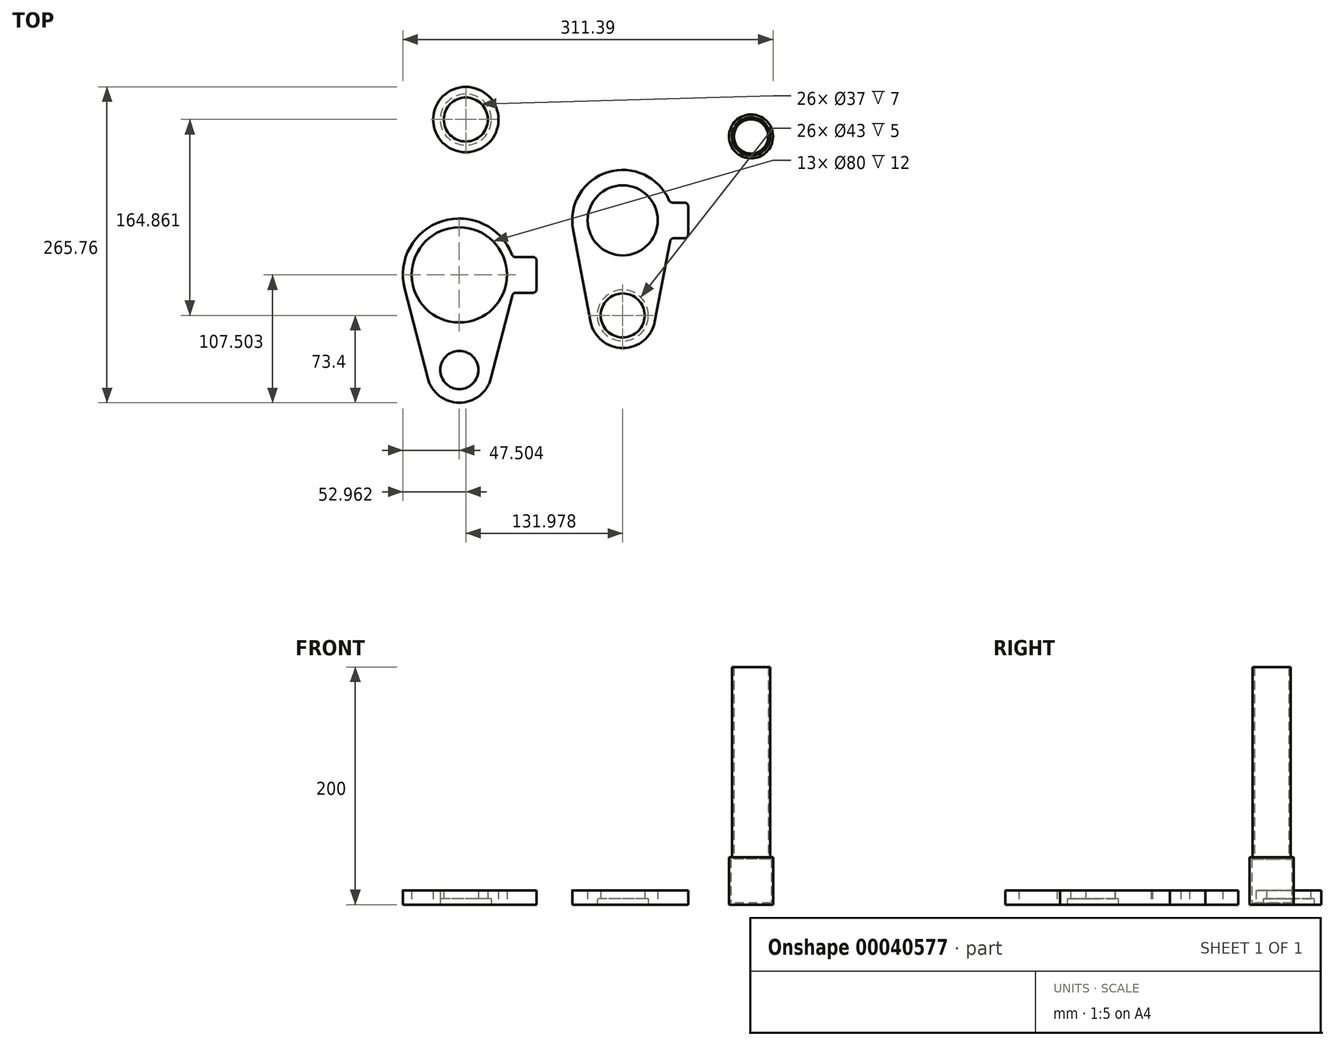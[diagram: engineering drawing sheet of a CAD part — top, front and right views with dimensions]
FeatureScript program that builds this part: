
annotation { "Feature Type Name" : "Feature", "Feature Type Description" : "" }
export const myFeature = defineFeature(function(context is Context, id is Id, definition is map)
    precondition{}
    {
        {
            var Q0;
            Q0=qCreatedBy(makeId("Top.planeOp"),FACE);
            var sketch = newSketch(context, id + "F0", { "sketchPlane" : qUnion([Q0])});
            skArc(sketch, "E0", {"start": v(29.46, 1.5) * mm, "mid": v(-29.5, 0) * mm, "end": v(29.46, -1.5) * mm});
            skArc(sketch, "E1", {"start": v(39.03, 16.81) * mm, "mid": v(-12.47, 40.63) * mm, "end": v(-41.75, -7.97) * mm});
            skCircle(sketch, "E2", {"center": v(0, -80) * mm, "radius": 18.5 * mm});
            skArc(sketch, "E3", {"start": v(-27.01, -85.16) * mm, "mid": v(0, -107.5) * mm, "end": v(27.01, -85.16) * mm});
            skLineSegment(sketch, "E4.left", {"start": v(55, 12) * mm, "end": v(55, 1.5) * mm});
            skLineSegment(sketch, "E5", {"start": v(52, 15) * mm, "end": v(41.79, 15) * mm});
            skLineSegment(sketch, "E6", {"start": v(-41.75, -7.97) * mm, "end": v(-27.01, -85.16) * mm});
            skLineSegment(sketch, "E7", {"start": v(39.94, -17.44) * mm, "end": v(27.01, -85.16) * mm});
            skLineSegment(sketch, "E8", {"start": v(52, -15) * mm, "end": v(42.89, -15) * mm});
            skPoint(sketch, "E4.right.start.orphan", {"position": v(-55, 50) * mm});
            skPoint(sketch, "E9.orphan", {"position": v(-55, -50) * mm});
            skPoint(sketch, "E10.orphan", {"position": v(55, -50) * mm});
            skPoint(sketch, "E11.orphan", {"position": v(55, 50) * mm});
            skPoint(sketch, "E12.visualSharp", {"position": v(55, 15) * mm});
            skArc(sketch, "E12.filletArc", {"start": v(55, 12) * mm, "mid": v(54.12, 14.12) * mm, "end": v(52, 15) * mm});
            skPoint(sketch, "E13.visualSharp", {"position": v(55, -15) * mm});
            skArc(sketch, "E13.filletArc", {"start": v(52, -15) * mm, "mid": v(54.12, -14.12) * mm, "end": v(55, -12) * mm});
            skArc(sketch, "E14.filletArc", {"start": v(42.89, -15) * mm, "mid": v(40.97, -15.69) * mm, "end": v(39.94, -17.44) * mm});
            skArc(sketch, "E15.filletArc", {"start": v(39.03, 16.81) * mm, "mid": v(40.14, 15.5) * mm, "end": v(41.79, 15) * mm});
            skLineSegment(sketch, "E16.trimOffspring", {"start": v(55, -1.5) * mm, "end": v(55, -12) * mm});
            skCircle(sketch, "E17", {"center": v(107.95, 70.65) * mm, "radius": 18.5 * mm});
            skLineSegment(sketch, "E18", {"start": v(55, 1.5) * mm, "end": v(55, -1.5) * mm});
            skArc(sketch, "E19", {"start": v(29.46, 1.5) * mm, "mid": v(29.5, 0) * mm, "end": v(29.46, -1.5) * mm});
            skArc(sketch, "E20", {"start": v(-97.49, -43.86) * mm, "mid": v(-177.44, -45.9) * mm, "end": v(-97.49, -47.93) * mm});
            skArc(sketch, "E21", {"start": v(-93.06, -28.97) * mm, "mid": v(-151.86, -0.64) * mm, "end": v(-183.43, -57.77) * mm});
            skCircle(sketch, "E22", {"center": v(-137.44, -125.9) * mm, "radius": 16.05 * mm});
            skArc(sketch, "E23", {"start": v(-164.06, -132.77) * mm, "mid": v(-137.44, -153.4) * mm, "end": v(-110.8, -132.77) * mm});
            skLineSegment(sketch, "E24.left", {"start": v(-72.44, -33.9) * mm, "end": v(-72.44, -44.4) * mm});
            skLineSegment(sketch, "E25", {"start": v(-75.44, -30.9) * mm, "end": v(-90.25, -30.9) * mm});
            skLineSegment(sketch, "E26", {"start": v(-183.43, -57.77) * mm, "end": v(-164.06, -132.77) * mm});
            skLineSegment(sketch, "E27", {"start": v(-92.83, -63.15) * mm, "end": v(-110.8, -132.77) * mm});
            skLineSegment(sketch, "E28", {"start": v(-75.44, -60.9) * mm, "end": v(-89.93, -60.9) * mm});
            skPoint(sketch, "E24.right.start.orphan", {"position": v(-202.44, 4.1) * mm});
            skPoint(sketch, "E29.orphan", {"position": v(-202.44, -104.99) * mm});
            skPoint(sketch, "E30.orphan", {"position": v(-72.44, -95.9) * mm});
            skPoint(sketch, "E31.orphan", {"position": v(-72.44, 13.2) * mm});
            skPoint(sketch, "E32.visualSharp", {"position": v(-72.44, -30.9) * mm});
            skArc(sketch, "E32.filletArc", {"start": v(-72.44, -33.9) * mm, "mid": v(-73.31, -31.78) * mm, "end": v(-75.44, -30.9) * mm});
            skPoint(sketch, "E33.visualSharp", {"position": v(-72.44, -60.9) * mm});
            skArc(sketch, "E33.filletArc", {"start": v(-75.44, -60.9) * mm, "mid": v(-73.31, -60.02) * mm, "end": v(-72.44, -57.9) * mm});
            skArc(sketch, "E34.filletArc", {"start": v(-89.93, -60.9) * mm, "mid": v(-91.76, -61.53) * mm, "end": v(-92.83, -63.15) * mm});
            skArc(sketch, "E35.filletArc", {"start": v(-93.06, -28.97) * mm, "mid": v(-91.95, -30.37) * mm, "end": v(-90.25, -30.9) * mm});
            skLineSegment(sketch, "E36.trimOffspring", {"start": v(-72.44, -47.4) * mm, "end": v(-72.44, -57.9) * mm});
            skLineSegment(sketch, "E37", {"start": v(-72.44, -44.4) * mm, "end": v(-72.44, -47.4) * mm});
            skArc(sketch, "E38", {"start": v(-97.49, -43.86) * mm, "mid": v(-97.44, -45.9) * mm, "end": v(-97.49, -47.93) * mm});
            skCircle(sketch, "E39", {"center": v(107.95, 70.65) * mm, "radius": 16 * mm});
            skCircle(sketch, "E40", {"center": v(-131.98, 84.86) * mm, "radius": 18.5 * mm});
            skCircle(sketch, "E41", {"center": v(-131.98, 84.86) * mm, "radius": 27.5 * mm});
            skCircle(sketch, "E42", {"center": v(0, -80) * mm, "radius": 21.5 * mm});
            skCircle(sketch, "E43", {"center": v(-131.98, 84.86) * mm, "radius": 21.5 * mm});
            skSolve(sketch);
        }
        {
            var Q0;
            Q0=makeQuery(id+"F0.imprint","IMPRINT",FACE,{"disambiguationData":[TD([[makeQuery(id+"F0.imprint","IMPRINT",EDGE,{"derivedFrom":sQuery(id+"F0.wireOp",EDGE,"E0")}),-1.0]])]});
            var Q1;
            Q1=makeQuery(id+"F0.imprint","IMPRINT",FACE,{"disambiguationData":[TD([[makeQuery(id+"F0.imprint","IMPRINT",EDGE,{"derivedFrom":sQuery(id+"F0.wireOp",EDGE,"E20")}),-1.0]])]});
            var Q2;
            Q2=makeQuery(id+"F0.imprint","IMPRINT",FACE,{"disambiguationData":[TD([[makeQuery(id+"F0.imprint","IMPRINT",EDGE,{"derivedFrom":sQuery(id+"F0.wireOp",EDGE,"E2")}),-1.0]])]});
            var Q3;
            Q3=makeQuery(id+"F0.imprint","IMPRINT",FACE,{"disambiguationData":[TD([[makeQuery(id+"F0.imprint","IMPRINT",EDGE,{"derivedFrom":sQuery(id+"F0.wireOp",EDGE,"E41")}),1.0]])]});
            var Q4;
            Q4=makeQuery(id+"F0.imprint","IMPRINT",FACE,{"disambiguationData":[TD([[makeQuery(id+"F0.imprint","IMPRINT",EDGE,{"derivedFrom":sQuery(id+"F0.wireOp",EDGE,"E40")}),-1.0]])]});
            extrude(context, id + "F1", {"entities" : qUnion([Q0, Q1, Q2, Q3, Q4]), "depth" : 12 * mm});
        }
        {
            var Q0;
            Q0=makeQuery(id+"F0.imprint","IMPRINT",FACE,{"disambiguationData":[TD([[makeQuery(id+"F0.imprint","IMPRINT",EDGE,{"derivedFrom":sQuery(id+"F0.wireOp",EDGE,"E39")}),1.0]])]});
            extrude(context, id + "F2", {"entities" : qUnion([Q0]), "depth" : 200 * mm});
        }
        {
            var Q0;
            Q0=makeQuery(id+"F0.imprint","IMPRINT",FACE,{"disambiguationData":[TD([[makeQuery(id+"F0.imprint","IMPRINT",EDGE,{"derivedFrom":sQuery(id+"F0.wireOp",EDGE,"E17")}),1.0]])]});
            extrude(context, id + "F3", {"entities" : qUnion([Q0]), "operationType" : NewBodyOperationType.ADD, "depth" : 40 * mm});
        }
        {
            var Q0;
            Q0=makeQuery(id+"F0.imprint","IMPRINT",FACE,{"disambiguationData":[TD([[makeQuery(id+"F0.imprint","IMPRINT",EDGE,{"derivedFrom":sQuery(id+"F0.wireOp",EDGE,"E2")}),-1.0]])]});
            extrude(context, id + "F4", {"entities" : qUnion([Q0]), "operationType" : NewBodyOperationType.REMOVE, "depth" : 5 * mm});
        }
        {
            var Q0;
            Q0=makeQuery(id+"F0.imprint","IMPRINT",FACE,{"disambiguationData":[TD([[makeQuery(id+"F0.imprint","IMPRINT",EDGE,{"derivedFrom":sQuery(id+"F0.wireOp",EDGE,"E40")}),-1.0]])]});
            extrude(context, id + "F5", {"entities" : qUnion([Q0]), "operationType" : NewBodyOperationType.REMOVE, "depth" : 5 * mm});
        }
        {
            var Q0;
            Q0=makeQuery(id+"F2.opExtrude","CAP_FACE",FACE,{"disambiguationData":[OSD([sQuery(id+"F0.wireOp",EDGE,"E39")])],"isStart":false});
            shell(context, id + "F6", {"entities" : qUnion([Q0]), "thickness" : 1.6 * mm});
        }
    });
